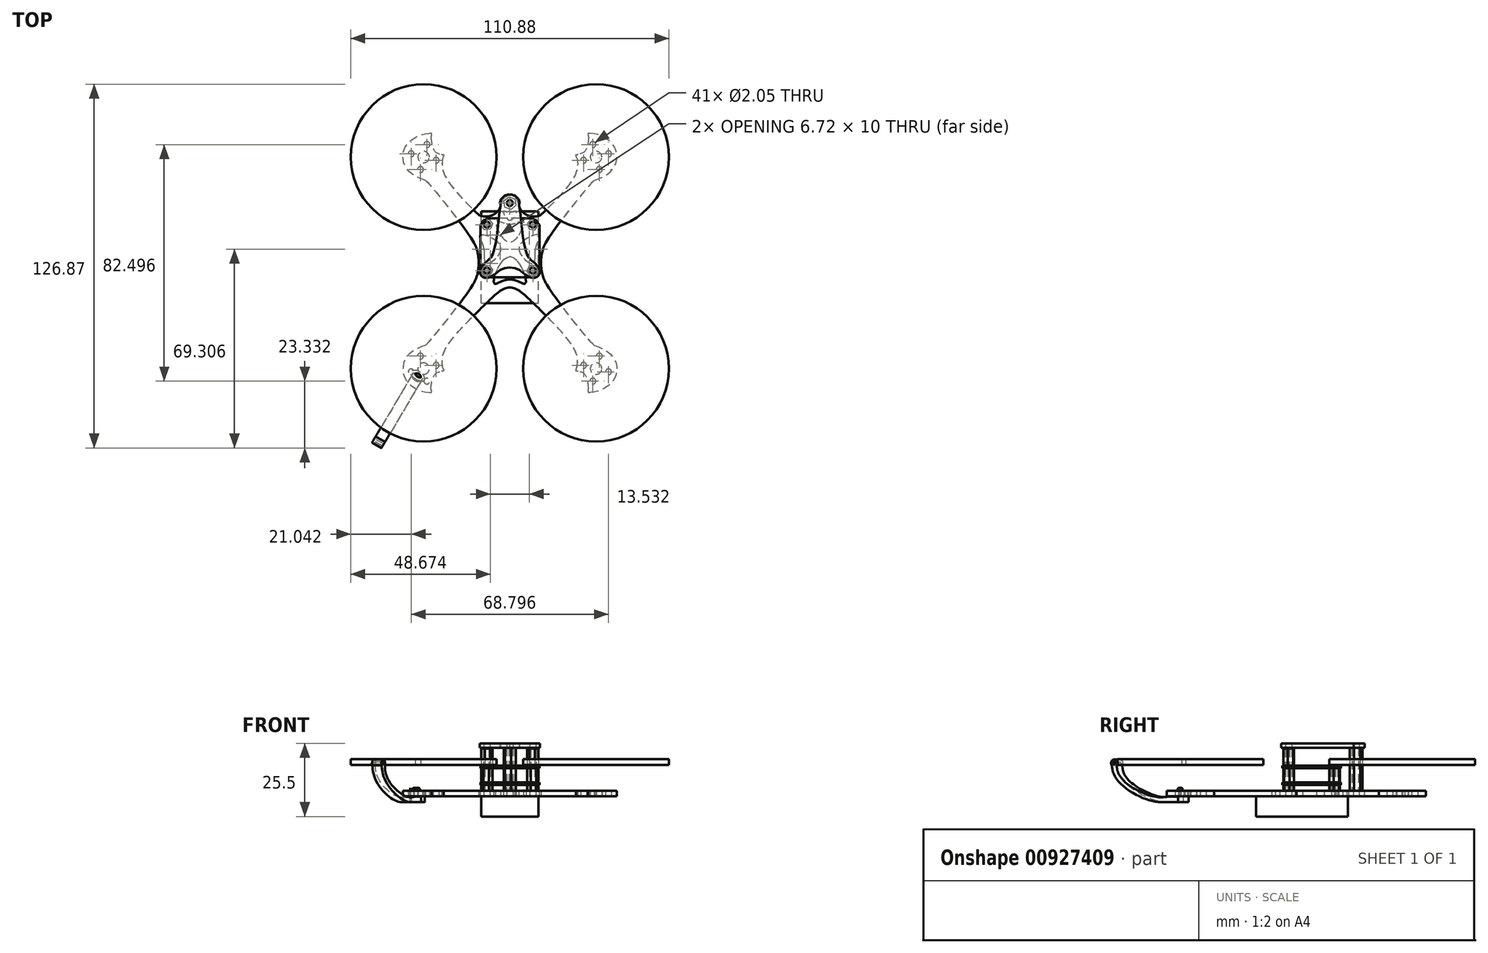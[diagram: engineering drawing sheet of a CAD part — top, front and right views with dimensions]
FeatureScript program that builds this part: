
annotation { "Feature Type Name" : "Feature", "Feature Type Description" : "" }
export const myFeature = defineFeature(function(context is Context, id is Id, definition is map)
    precondition{}
    {
        {
            assignVariable(context, id + "F0", {"name" : "PlateThickness", "anyValue" : 2 * mm});
        }
        {
            assignVariable(context, id + "F1", {"name" : "StackHeight", "lengthValue" : 15 * mm, "variableType" : VariableType.LENGTH});
        }
        {
            assignVariable(context, id + "F2", {"name" : "FCThickness", "anyValue" : 0.85 * mm});
        }
        {
            assignVariable(context, id + "F3", {"name" : "FCSpacerHeight", "anyValue" : 2 * mm});
        }
        {
            assignVariable(context, id + "F4", {"name" : "ESCStandoffHeight", "anyValue" : 5 * mm});
        }
        {
            var Q0;
            Q0=qCreatedBy(makeId("Top.planeOp"),FACE);
            var sketch = newSketch(context, id + "F5", { "sketchPlane" : qUnion([Q0])});
            skLineSegment(sketch, "E0", {"start": v(30.04, 36.9) * mm, "end": v(-30.04, -36.9) * mm, "construction": true});
            skLineSegment(sketch, "E1", {"start": v(-30.04, 36.9) * mm, "end": v(30.04, -36.9) * mm, "construction": true});
            skCircle(sketch, "E2", {"center": v(30.04, 36.9) * mm, "radius": 25.4 * mm, "construction": true});
            skCircle(sketch, "E3", {"center": v(-30.04, 36.9) * mm, "radius": 25.4 * mm, "construction": true});
            skCircle(sketch, "E4", {"center": v(-30.04, -36.9) * mm, "radius": 25.4 * mm, "construction": true});
            skCircle(sketch, "E5", {"center": v(30.04, -36.9) * mm, "radius": 25.4 * mm, "construction": true});
            skLineSegment(sketch, "E6", {"start": v(38.92, 31.66) * mm, "end": v(21.16, 42.12) * mm, "construction": true});
            skLineSegment(sketch, "E7", {"start": v(40.02, 39.47) * mm, "end": v(20.06, 34.31) * mm, "construction": true});
            skLineSegment(sketch, "E8", {"start": v(27.46, 46.87) * mm, "end": v(32.62, 26.91) * mm, "construction": true});
            skCircle(sketch, "E9", {"center": v(30.04, 36.9) * mm, "radius": 4.5 * mm, "construction": true});
            skCircle(sketch, "E10", {"center": v(28.91, 41.25) * mm, "radius": 1.02 * mm});
            skCircle(sketch, "E11", {"center": v(25.68, 35.76) * mm, "radius": 1.02 * mm});
            skCircle(sketch, "E12", {"center": v(31.17, 32.53) * mm, "radius": 1.02 * mm});
            skCircle(sketch, "E13", {"center": v(34.4, 38.02) * mm, "radius": 1.02 * mm});
            skCircle(sketch, "E14", {"center": v(-8, 13.3) * mm, "radius": 1.02 * mm});
            skCircle(sketch, "E15", {"center": v(8, 13.3) * mm, "radius": 1.02 * mm});
            skCircle(sketch, "E16", {"center": v(8, -2.7) * mm, "radius": 1.02 * mm});
            skCircle(sketch, "E17", {"center": v(-8, -2.7) * mm, "radius": 1.02 * mm});
            skCircle(sketch, "E18.MirrorC", {"center": v(-25.68, 35.76) * mm, "radius": 1.02 * mm});
            skCircle(sketch, "E19.MirrorC", {"center": v(-28.91, 41.25) * mm, "radius": 1.02 * mm});
            skCircle(sketch, "E20.MirrorC", {"center": v(-34.4, 38.02) * mm, "radius": 1.02 * mm});
            skCircle(sketch, "E21.MirrorC", {"center": v(-31.17, 32.53) * mm, "radius": 1.02 * mm});
            skCircle(sketch, "E22.MirrorC", {"center": v(-31.17, -32.53) * mm, "radius": 1.02 * mm});
            skCircle(sketch, "E23.MirrorC", {"center": v(-34.4, -38.02) * mm, "radius": 1.02 * mm});
            skCircle(sketch, "E24.MirrorC", {"center": v(-28.91, -41.25) * mm, "radius": 1.02 * mm});
            skCircle(sketch, "E25.MirrorC", {"center": v(-25.68, -35.76) * mm, "radius": 1.02 * mm});
            skCircle(sketch, "E26.MirrorC", {"center": v(25.68, -35.76) * mm, "radius": 1.02 * mm});
            skCircle(sketch, "E27.MirrorC", {"center": v(31.17, -32.53) * mm, "radius": 1.02 * mm});
            skCircle(sketch, "E28.MirrorC", {"center": v(34.4, -38.02) * mm, "radius": 1.02 * mm});
            skCircle(sketch, "E29.MirrorC", {"center": v(28.91, -41.25) * mm, "radius": 1.02 * mm});
            skFitSpline(sketch, "E30", {"points": [v(29.41, 28.73) * mm, v(34.84, 31.56) * mm, v(37.18, 38.3) * mm, v(34.2, 42.9) * mm, v(27.3, 45.15) * mm], "startDerivative": vector(4.7, 2.99) * mm, "endDerivative": vector(-30.23, -2.2) * mm});
            skFitSpline(sketch, "E31", {"points": [v(27.3, 45.15) * mm, v(26.58, 39.57) * mm, v(23, 37.72) * mm], "startDerivative": vector(1.88, -8.22) * mm, "endDerivative": vector(-12.25, -1.45) * mm});
            skFitSpline(sketch, "E32", {"points": [v(23, 37.72) * mm, v(23.04, 31.32) * mm, v(8.78, 14.66) * mm, v(0, 8.59) * mm], "startDerivative": vector(6.6, -21.28) * mm, "endDerivative": vector(-26.5, 0) * mm});
            skFitSpline(sketch, "E33", {"points": [v(29.41, 28.73) * mm, v(14.08, 9.46) * mm, v(10.83, 0) * mm], "startDerivative": vector(-5.44, -3.2) * mm, "endDerivative": vector(-1.35, -29.87) * mm});
            skArc(sketch, "E34.filletArc", {"start": v(28.18, 45.17) * mm, "mid": v(27.62, 44.93) * mm, "end": v(27.41, 44.36) * mm});
            skArc(sketch, "E35.filletArc", {"start": v(23.83, 37.84) * mm, "mid": v(23.33, 37.5) * mm, "end": v(23.24, 36.9) * mm});
            skFitSpline(sketch, "E36.MirrorCS", {"points": [v(29.41, -28.73) * mm, v(14.08, -9.46) * mm, v(10.83, 0) * mm], "startDerivative": vector(-5.44, 3.2) * mm, "endDerivative": vector(-1.35, 29.87) * mm});
            skFitSpline(sketch, "E37.MirrorCS", {"points": [v(23, -37.72) * mm, v(23.04, -31.32) * mm, v(8.78, -14.66) * mm, v(0, -8.59) * mm], "startDerivative": vector(6.6, 21.28) * mm, "endDerivative": vector(-26.5, 0) * mm});
            skArc(sketch, "E38.MirrorCS", {"start": v(23.83, -37.84) * mm, "mid": v(23.33, -37.5) * mm, "end": v(23.24, -36.9) * mm});
            skFitSpline(sketch, "E39.MirrorCS", {"points": [v(27.3, -45.15) * mm, v(26.58, -39.57) * mm, v(23, -37.72) * mm], "startDerivative": vector(1.88, 8.22) * mm, "endDerivative": vector(-12.25, 1.45) * mm});
            skArc(sketch, "E40.MirrorCS", {"start": v(28.18, -45.17) * mm, "mid": v(27.62, -44.93) * mm, "end": v(27.41, -44.36) * mm});
            skFitSpline(sketch, "E41.MirrorCS", {"points": [v(29.41, -28.73) * mm, v(34.84, -31.56) * mm, v(37.18, -38.3) * mm, v(34.2, -42.9) * mm, v(27.3, -45.15) * mm], "startDerivative": vector(4.7, -2.99) * mm, "endDerivative": vector(-30.23, 2.2) * mm});
            skCircle(sketch, "E42", {"center": v(30.04, 36.9) * mm, "radius": 2 * mm});
            skCircle(sketch, "E43.MirrorC", {"center": v(30.04, -36.9) * mm, "radius": 2 * mm});
            skFitSpline(sketch, "E44.MirrorCS", {"points": [v(-29.41, -28.73) * mm, v(-34.84, -31.56) * mm, v(-37.18, -38.3) * mm, v(-34.2, -42.9) * mm, v(-27.3, -45.15) * mm], "startDerivative": vector(-4.7, -2.99) * mm, "endDerivative": vector(30.23, 2.2) * mm});
            skFitSpline(sketch, "E45.MirrorCS", {"points": [v(-27.3, -45.15) * mm, v(-26.58, -39.57) * mm, v(-23, -37.72) * mm], "startDerivative": vector(-1.88, 8.22) * mm, "endDerivative": vector(12.25, 1.45) * mm});
            skArc(sketch, "E46.MirrorCS", {"start": v(-28.18, -45.17) * mm, "mid": v(-27.62, -44.93) * mm, "end": v(-27.41, -44.36) * mm});
            skArc(sketch, "E47.MirrorCS", {"start": v(-23.83, -37.84) * mm, "mid": v(-23.33, -37.5) * mm, "end": v(-23.24, -36.9) * mm});
            skFitSpline(sketch, "E48.MirrorCS", {"points": [v(-23, -37.72) * mm, v(-23.04, -31.32) * mm, v(-8.78, -14.66) * mm, v(0, -8.59) * mm], "startDerivative": vector(-6.6, 21.28) * mm, "endDerivative": vector(26.5, 0) * mm});
            skFitSpline(sketch, "E49.MirrorCS", {"points": [v(-29.41, -28.73) * mm, v(-14.08, -9.46) * mm, v(-10.83, 0) * mm], "startDerivative": vector(5.44, 3.2) * mm, "endDerivative": vector(1.35, 29.87) * mm});
            skCircle(sketch, "E50.MirrorC", {"center": v(-30.04, -36.9) * mm, "radius": 2 * mm});
            skFitSpline(sketch, "E51.MirrorCS", {"points": [v(-29.41, 28.73) * mm, v(-14.08, 9.46) * mm, v(-10.83, 0) * mm], "startDerivative": vector(5.44, -3.2) * mm, "endDerivative": vector(1.35, -29.87) * mm});
            skFitSpline(sketch, "E52.MirrorCS", {"points": [v(-29.41, 28.73) * mm, v(-34.84, 31.56) * mm, v(-37.18, 38.3) * mm, v(-34.2, 42.9) * mm, v(-27.3, 45.15) * mm], "startDerivative": vector(-4.7, 2.99) * mm, "endDerivative": vector(30.23, -2.2) * mm});
            skArc(sketch, "E53.MirrorCS", {"start": v(-28.18, 45.17) * mm, "mid": v(-27.62, 44.93) * mm, "end": v(-27.41, 44.36) * mm});
            skFitSpline(sketch, "E54.MirrorCS", {"points": [v(-27.3, 45.15) * mm, v(-26.58, 39.57) * mm, v(-23, 37.72) * mm], "startDerivative": vector(-1.88, -8.22) * mm, "endDerivative": vector(12.25, -1.45) * mm});
            skArc(sketch, "E55.MirrorCS", {"start": v(-23.83, 37.84) * mm, "mid": v(-23.33, 37.5) * mm, "end": v(-23.24, 36.9) * mm});
            skFitSpline(sketch, "E56.MirrorCS", {"points": [v(-23, 37.72) * mm, v(-23.04, 31.32) * mm, v(-8.78, 14.66) * mm, v(0, 8.59) * mm], "startDerivative": vector(-6.6, -21.28) * mm, "endDerivative": vector(26.5, 0) * mm});
            skCircle(sketch, "E57.MirrorC", {"center": v(-30.04, 36.9) * mm, "radius": 2 * mm});
            skFitSpline(sketch, "E58", {"points": [v(10.08, 9.75) * mm, v(3.22, 5.3) * mm, v(8.08, -0.3) * mm, v(9, 4.92) * mm, v(10.08, 9.75) * mm]});
            skFitSpline(sketch, "E59.MirrorC", {"points": [v(-10.08, 9.75) * mm, v(-3.22, 5.3) * mm, v(-8.08, -0.3) * mm, v(-9, 4.92) * mm, v(-10.08, 9.75) * mm]});
            skFitSpline(sketch, "E60.MirrorC", {"points": [v(0, 2.19) * mm, v(5.5, -7.02) * mm, v(0, -5.75) * mm, v(-5.5, -7.02) * mm, v(0, 2.19) * mm]});
            skFitSpline(sketch, "E61", {"points": [v(31.89, 39.83) * mm, v(34.14, 40.16) * mm, v(32.64, 42.18) * mm, v(30.86, 42.04) * mm, v(31.89, 39.83) * mm], "construction": true});
            skFitSpline(sketch, "E62", {"points": [v(33.63, 36.26) * mm, v(32.54, 35.08) * mm, v(33.08, 33.36) * mm, v(34.42, 34.31) * mm, v(34.82, 35.96) * mm, v(33.63, 36.26) * mm], "construction": true});
            skLineSegment(sketch, "E63", {"start": v(17.83, 16.16) * mm, "end": v(35.03, 45.37) * mm, "construction": true});
            skFitSpline(sketch, "E64.MirrorC", {"points": [v(-31.89, 39.83) * mm, v(-34.14, 40.16) * mm, v(-32.64, 42.18) * mm, v(-30.86, 42.04) * mm, v(-31.89, 39.83) * mm], "construction": true});
            skFitSpline(sketch, "E65.MirrorC", {"points": [v(-33.63, 36.26) * mm, v(-32.54, 35.08) * mm, v(-33.08, 33.36) * mm, v(-34.42, 34.31) * mm, v(-34.82, 35.96) * mm, v(-33.63, 36.26) * mm], "construction": true});
            skFitSpline(sketch, "E66.MirrorC", {"points": [v(33.63, -36.26) * mm, v(32.54, -35.08) * mm, v(33.08, -33.36) * mm, v(34.42, -34.31) * mm, v(34.82, -35.96) * mm, v(33.63, -36.26) * mm], "construction": true});
            skFitSpline(sketch, "E67.MirrorC", {"points": [v(31.89, -39.83) * mm, v(34.14, -40.16) * mm, v(32.64, -42.18) * mm, v(30.86, -42.04) * mm, v(31.89, -39.83) * mm], "construction": true});
            skFitSpline(sketch, "E68.MirrorC", {"points": [v(-31.89, -39.83) * mm, v(-34.14, -40.16) * mm, v(-32.64, -42.18) * mm, v(-30.86, -42.04) * mm, v(-31.89, -39.83) * mm], "construction": true});
            skFitSpline(sketch, "E69.MirrorC", {"points": [v(-33.63, -36.26) * mm, v(-32.54, -35.08) * mm, v(-33.08, -33.36) * mm, v(-34.42, -34.31) * mm, v(-34.82, -35.96) * mm, v(-33.63, -36.26) * mm], "construction": true});
            skCircle(sketch, "E70", {"center": v(0, 20.84) * mm, "radius": 1.02 * mm});
            skFitSpline(sketch, "E71", {"points": [v(-11.69, 17.5) * mm, v(-4.28, 17.9) * mm, v(-2.63, 21.6) * mm, v(0, 23.7) * mm], "startDerivative": vector(17.88, -17.8) * mm, "endDerivative": vector(10.8, -0.04) * mm});
            skFitSpline(sketch, "E72.MirrorCS", {"points": [v(11.69, 17.5) * mm, v(4.28, 17.9) * mm, v(2.63, 21.6) * mm, v(0, 23.7) * mm], "startDerivative": vector(-17.88, -17.8) * mm, "endDerivative": vector(-10.8, -0.04) * mm});
            skLineSegment(sketch, "E73", {"start": v(27.93, 47.57) * mm, "end": v(40.4, 40.22) * mm, "construction": true});
            skPoint(sketch, "E74", {"position": v(34.17, 43.9) * mm});
            skLineSegment(sketch, "E75", {"start": v(40.4, 40.22) * mm, "end": v(33.06, 27.74) * mm, "construction": true});
            skLineSegment(sketch, "E76", {"start": v(27.93, 47.57) * mm, "end": v(20.58, 35.1) * mm, "construction": true});
            skLineSegment(sketch, "E77", {"start": v(33.06, 27.74) * mm, "end": v(20.58, 35.1) * mm, "construction": true});
            skLineSegment(sketch, "E78", {"start": v(8, 13.3) * mm, "end": v(-8, -2.7) * mm, "construction": true});
            skLineSegment(sketch, "E79", {"start": v(8, -2.7) * mm, "end": v(-8, 13.3) * mm, "construction": true});
            skPoint(sketch, "E80", {"position": v(0, 5.3) * mm});
            skLineSegment(sketch, "E81", {"start": v(-2.38, 5.3) * mm, "end": v(2.38, 5.3) * mm, "construction": true});
            skFitSpline(sketch, "E82.MirrorC", {"points": [v(0, 7.2) * mm, v(4.88, 14.48) * mm, v(0, 13.35) * mm, v(-4.88, 14.48) * mm, v(0, 7.2) * mm]});
            skFitSpline(sketch, "E83", {"points": [v(0, 17.57) * mm, v(2.16, 18.06) * mm, v(0, 14.71) * mm, v(-2.16, 18.06) * mm, v(0, 17.57) * mm]});
            skFitSpline(sketch, "E84", {"points": [v(-8.8, 1.66) * mm, v(-7.94, 2.3) * mm, v(-6.94, 1.65) * mm, v(-6.44, 3.35) * mm, v(-6.94, 5.05) * mm, v(-7.94, 4.4) * mm, v(-8.94, 4.63) * mm], "startDerivative": vector(0.09, 5.2) * mm, "endDerivative": vector(-0.67, 5.38) * mm});
            skLineSegment(sketch, "E85", {"start": v(-6.2, 3.35) * mm, "end": v(-9.6, 3.35) * mm, "construction": true});
            skFitSpline(sketch, "E86.MirrorCS", {"points": [v(8.8, 1.66) * mm, v(7.94, 2.3) * mm, v(6.94, 1.65) * mm, v(6.44, 3.35) * mm, v(6.94, 5.05) * mm, v(7.94, 4.4) * mm, v(8.94, 4.63) * mm], "startDerivative": vector(-0.09, 5.2) * mm, "endDerivative": vector(0.67, 5.38) * mm});
            skFitSpline(sketch, "E87", {"points": [v(1.82, -6.1) * mm, v(1.05, -5.1) * mm, v(1.7, -4.1) * mm, v(0, -3.6) * mm, v(-1.7, -4.1) * mm, v(-1.05, -5.1) * mm, v(-1.82, -6.1) * mm], "startDerivative": vector(-10.77, 5.24) * mm, "endDerivative": vector(-10.77, -5.24) * mm});
            skFitSpline(sketch, "E88", {"points": [v(-1.82, 13.7) * mm, v(-1.05, 12.7) * mm, v(-1.7, 11.7) * mm, v(0, 11.2) * mm, v(1.7, 11.7) * mm, v(1.05, 12.7) * mm, v(1.82, 13.7) * mm], "startDerivative": vector(3.97, -1.14) * mm, "endDerivative": vector(3.92, 1.03) * mm});
            skCircle(sketch, "E89", {"center": v(30.04, 36.9) * mm, "radius": 6.75 * mm, "construction": true});
            skSolve(sketch);
        }
        {
            var Q0;
            Q0=qSketchRegion(id+"F5",true);
            extrude(context, id + "F6", {"entities" : qUnion([Q0]), "depth" : getVariable(context, 'PlateThickness'), "offsetDistance" : 25 * mm});
        }
        {
            var Q0;
            Q0=makeQuery(id+"F6.opExtrude","CAP_FACE",FACE,{"disambiguationData":[OSD([sQuery(id+"F5.wireOp",EDGE,"E10"),sQuery(id+"F5.wireOp",EDGE,"E11"),sQuery(id+"F5.wireOp",EDGE,"E12"),sQuery(id+"F5.wireOp",EDGE,"E13"),sQuery(id+"F5.wireOp",EDGE,"E14"),sQuery(id+"F5.wireOp",EDGE,"E15"),sQuery(id+"F5.wireOp",EDGE,"E16"),sQuery(id+"F5.wireOp",EDGE,"E17"),sQuery(id+"F5.wireOp",EDGE,"E18.MirrorC"),sQuery(id+"F5.wireOp",EDGE,"E19.MirrorC"),sQuery(id+"F5.wireOp",EDGE,"E20.MirrorC"),sQuery(id+"F5.wireOp",EDGE,"E21.MirrorC"),sQuery(id+"F5.wireOp",EDGE,"E25.MirrorC"),sQuery(id+"F5.wireOp",EDGE,"E26.MirrorC"),sQuery(id+"F5.wireOp",EDGE,"E27.MirrorC"),sQuery(id+"F5.wireOp",EDGE,"E28.MirrorC"),sQuery(id+"F5.wireOp",EDGE,"E29.MirrorC"),sQuery(id+"F5.wireOp",EDGE,"E30"),sQuery(id+"F5.wireOp",EDGE,"E31"),sQuery(id+"F5.wireOp",EDGE,"E32"),sQuery(id+"F5.wireOp",EDGE,"E33"),sQuery(id+"F5.wireOp",EDGE,"E34.filletArc"),sQuery(id+"F5.wireOp",EDGE,"E35.filletArc"),sQuery(id+"F5.wireOp",EDGE,"E36.MirrorCS"),sQuery(id+"F5.wireOp",EDGE,"E37.MirrorCS"),sQuery(id+"F5.wireOp",EDGE,"E38.MirrorCS"),sQuery(id+"F5.wireOp",EDGE,"E39.MirrorCS"),sQuery(id+"F5.wireOp",EDGE,"E40.MirrorCS"),sQuery(id+"F5.wireOp",EDGE,"E41.MirrorCS"),sQuery(id+"F5.wireOp",EDGE,"E42"),sQuery(id+"F5.wireOp",EDGE,"E43.MirrorC"),sQuery(id+"F5.wireOp",EDGE,"E23.MirrorC"),sQuery(id+"F5.wireOp",EDGE,"E44.MirrorCS"),sQuery(id+"F5.wireOp",EDGE,"E22.MirrorC"),sQuery(id+"F5.wireOp",EDGE,"E24.MirrorC"),sQuery(id+"F5.wireOp",EDGE,"E45.MirrorCS"),sQuery(id+"F5.wireOp",EDGE,"E46.MirrorCS"),sQuery(id+"F5.wireOp",EDGE,"E47.MirrorCS"),sQuery(id+"F5.wireOp",EDGE,"E48.MirrorCS"),sQuery(id+"F5.wireOp",EDGE,"E49.MirrorCS"),sQuery(id+"F5.wireOp",EDGE,"E50.MirrorC"),sQuery(id+"F5.wireOp",EDGE,"E51.MirrorCS"),sQuery(id+"F5.wireOp",EDGE,"E52.MirrorCS"),sQuery(id+"F5.wireOp",EDGE,"E53.MirrorCS"),sQuery(id+"F5.wireOp",EDGE,"E54.MirrorCS"),sQuery(id+"F5.wireOp",EDGE,"E55.MirrorCS"),sQuery(id+"F5.wireOp",EDGE,"E56.MirrorCS"),sQuery(id+"F5.wireOp",EDGE,"E57.MirrorC"),sQuery(id+"F5.wireOp",EDGE,"E58"),sQuery(id+"F5.wireOp",EDGE,"E59.MirrorC"),sQuery(id+"F5.wireOp",EDGE,"dcd4970c-f5e5-4935-b7b6-60d1fb3fb8a0"),sQuery(id+"F5.wireOp",EDGE,"E60.MirrorC"),sQuery(id+"F5.wireOp",EDGE,"E61"),sQuery(id+"F5.wireOp",EDGE,"E62")])],"isStart":false});
            var sketch = newSketch(context, id + "F7", { "sketchPlane" : qUnion([Q0])});
            skCircle(sketch, "E90.cCircle", {"center": v(-8, 13.3) * mm, "radius": 2 * mm, "construction": true});
            skLineSegment(sketch, "E90.0", {"start": v(-9.24, 14.88) * mm, "end": v(-7.26, 15.16) * mm});
            skLineSegment(sketch, "E90.1", {"start": v(-7.26, 15.16) * mm, "end": v(-6.02, 13.59) * mm});
            skLineSegment(sketch, "E90.2", {"start": v(-6.02, 13.59) * mm, "end": v(-6.76, 11.73) * mm});
            skLineSegment(sketch, "E90.3", {"start": v(-6.76, 11.73) * mm, "end": v(-8.74, 11.45) * mm});
            skLineSegment(sketch, "E90.4", {"start": v(-8.74, 11.45) * mm, "end": v(-9.98, 13.02) * mm});
            skLineSegment(sketch, "E90.5", {"start": v(-9.98, 13.02) * mm, "end": v(-9.24, 14.88) * mm});
            skLineSegment(sketch, "E91.MirrorCS", {"start": v(9.98, 13.02) * mm, "end": v(9.24, 14.88) * mm});
            skLineSegment(sketch, "E92.MirrorCS", {"start": v(7.26, 15.16) * mm, "end": v(6.02, 13.59) * mm});
            skLineSegment(sketch, "E93.MirrorCS", {"start": v(6.02, 13.59) * mm, "end": v(6.76, 11.73) * mm});
            skCircle(sketch, "E94.MirrorC", {"center": v(8, 13.3) * mm, "radius": 2 * mm, "construction": true});
            skLineSegment(sketch, "E95.MirrorCS", {"start": v(8.74, 11.45) * mm, "end": v(9.98, 13.02) * mm});
            skLineSegment(sketch, "E96.MirrorCS", {"start": v(6.76, 11.73) * mm, "end": v(8.74, 11.45) * mm});
            skLineSegment(sketch, "E97.MirrorCS", {"start": v(9.24, 14.88) * mm, "end": v(7.26, 15.16) * mm});
            skCircle(sketch, "E98.0", {"center": v(-8, 13.3) * mm, "radius": 1.02 * mm});
            skCircle(sketch, "E99.0", {"center": v(8, 13.3) * mm, "radius": 1.02 * mm});
            skCircle(sketch, "E100.0", {"center": v(8, -2.7) * mm, "radius": 1.02 * mm});
            skCircle(sketch, "E101.0", {"center": v(-8, -2.7) * mm, "radius": 1.02 * mm});
            skLineSegment(sketch, "E102.MirrorCS", {"start": v(-9.24, -4.27) * mm, "end": v(-7.26, -4.55) * mm});
            skLineSegment(sketch, "E103.MirrorCS", {"start": v(-9.98, -2.41) * mm, "end": v(-9.24, -4.27) * mm});
            skLineSegment(sketch, "E104.MirrorCS", {"start": v(-7.26, -4.55) * mm, "end": v(-6.02, -2.98) * mm});
            skLineSegment(sketch, "E105.MirrorCS", {"start": v(-6.02, -2.98) * mm, "end": v(-6.76, -1.12) * mm});
            skLineSegment(sketch, "E106.MirrorCS", {"start": v(-6.76, -1.12) * mm, "end": v(-8.74, -0.84) * mm});
            skLineSegment(sketch, "E107.MirrorCS", {"start": v(-8.74, -0.84) * mm, "end": v(-9.98, -2.41) * mm});
            skLineSegment(sketch, "E108.MirrorCS", {"start": v(7.26, -4.55) * mm, "end": v(6.02, -2.98) * mm});
            skLineSegment(sketch, "E109.MirrorCS", {"start": v(9.24, -4.27) * mm, "end": v(7.26, -4.55) * mm});
            skLineSegment(sketch, "E110.MirrorCS", {"start": v(9.98, -2.41) * mm, "end": v(9.24, -4.27) * mm});
            skLineSegment(sketch, "E111.MirrorCS", {"start": v(8.74, -0.84) * mm, "end": v(9.98, -2.41) * mm});
            skLineSegment(sketch, "E112.MirrorCS", {"start": v(6.76, -1.12) * mm, "end": v(8.74, -0.84) * mm});
            skLineSegment(sketch, "E113.MirrorCS", {"start": v(6.02, -2.98) * mm, "end": v(6.76, -1.12) * mm});
            skSolve(sketch);
        }
        {
            var Q0;
            Q0=qSketchRegion(id+"F7",true);
            extrude(context, id + "F8", {"entities" : qUnion([Q0]), "depth" : getVariable(context, 'FCSpacerHeight'), "offsetDistance" : 25 * mm});
        }
        {
            var Q0;
            Q0=makeQuery(id+"F6.opExtrude","CAP_FACE",FACE,{"disambiguationData":[OSD([sQuery(id+"F5.wireOp",EDGE,"E10"),sQuery(id+"F5.wireOp",EDGE,"E11"),sQuery(id+"F5.wireOp",EDGE,"E12"),sQuery(id+"F5.wireOp",EDGE,"E13"),sQuery(id+"F5.wireOp",EDGE,"E14"),sQuery(id+"F5.wireOp",EDGE,"E15"),sQuery(id+"F5.wireOp",EDGE,"E16"),sQuery(id+"F5.wireOp",EDGE,"E17"),sQuery(id+"F5.wireOp",EDGE,"E18.MirrorC"),sQuery(id+"F5.wireOp",EDGE,"E19.MirrorC"),sQuery(id+"F5.wireOp",EDGE,"E20.MirrorC"),sQuery(id+"F5.wireOp",EDGE,"E21.MirrorC"),sQuery(id+"F5.wireOp",EDGE,"E25.MirrorC"),sQuery(id+"F5.wireOp",EDGE,"E26.MirrorC"),sQuery(id+"F5.wireOp",EDGE,"E27.MirrorC"),sQuery(id+"F5.wireOp",EDGE,"E28.MirrorC"),sQuery(id+"F5.wireOp",EDGE,"E29.MirrorC"),sQuery(id+"F5.wireOp",EDGE,"E30"),sQuery(id+"F5.wireOp",EDGE,"E31"),sQuery(id+"F5.wireOp",EDGE,"E32"),sQuery(id+"F5.wireOp",EDGE,"E33"),sQuery(id+"F5.wireOp",EDGE,"E34.filletArc"),sQuery(id+"F5.wireOp",EDGE,"E35.filletArc"),sQuery(id+"F5.wireOp",EDGE,"E36.MirrorCS"),sQuery(id+"F5.wireOp",EDGE,"E37.MirrorCS"),sQuery(id+"F5.wireOp",EDGE,"E38.MirrorCS"),sQuery(id+"F5.wireOp",EDGE,"E39.MirrorCS"),sQuery(id+"F5.wireOp",EDGE,"E40.MirrorCS"),sQuery(id+"F5.wireOp",EDGE,"E41.MirrorCS"),sQuery(id+"F5.wireOp",EDGE,"E42"),sQuery(id+"F5.wireOp",EDGE,"E43.MirrorC"),sQuery(id+"F5.wireOp",EDGE,"E23.MirrorC"),sQuery(id+"F5.wireOp",EDGE,"E44.MirrorCS"),sQuery(id+"F5.wireOp",EDGE,"E22.MirrorC"),sQuery(id+"F5.wireOp",EDGE,"E24.MirrorC"),sQuery(id+"F5.wireOp",EDGE,"E45.MirrorCS"),sQuery(id+"F5.wireOp",EDGE,"E46.MirrorCS"),sQuery(id+"F5.wireOp",EDGE,"E47.MirrorCS"),sQuery(id+"F5.wireOp",EDGE,"E48.MirrorCS"),sQuery(id+"F5.wireOp",EDGE,"E49.MirrorCS"),sQuery(id+"F5.wireOp",EDGE,"E50.MirrorC"),sQuery(id+"F5.wireOp",EDGE,"E51.MirrorCS"),sQuery(id+"F5.wireOp",EDGE,"E52.MirrorCS"),sQuery(id+"F5.wireOp",EDGE,"E53.MirrorCS"),sQuery(id+"F5.wireOp",EDGE,"E54.MirrorCS"),sQuery(id+"F5.wireOp",EDGE,"E55.MirrorCS"),sQuery(id+"F5.wireOp",EDGE,"E56.MirrorCS"),sQuery(id+"F5.wireOp",EDGE,"E57.MirrorC"),sQuery(id+"F5.wireOp",EDGE,"E58"),sQuery(id+"F5.wireOp",EDGE,"E59.MirrorC"),sQuery(id+"F5.wireOp",EDGE,"dcd4970c-f5e5-4935-b7b6-60d1fb3fb8a0"),sQuery(id+"F5.wireOp",EDGE,"E60.MirrorC"),sQuery(id+"F5.wireOp",EDGE,"E61"),sQuery(id+"F5.wireOp",EDGE,"E62"),sQuery(id+"F5.wireOp",EDGE,"E64.MirrorC"),sQuery(id+"F5.wireOp",EDGE,"E65.MirrorC"),sQuery(id+"F5.wireOp",EDGE,"E66.MirrorC"),sQuery(id+"F5.wireOp",EDGE,"E67.MirrorC"),sQuery(id+"F5.wireOp",EDGE,"E68.MirrorC"),sQuery(id+"F5.wireOp",EDGE,"E69.MirrorC"),sQuery(id+"F5.wireOp",EDGE,"E70"),sQuery(id+"F5.wireOp",EDGE,"E71"),sQuery(id+"F5.wireOp",EDGE,"E72.MirrorCS"),sQuery(id+"F5.wireOp",EDGE,"54bec6d1-b576-4d2f-8366-efb064a77230")])],"isStart":false});
            var sketch = newSketch(context, id + "F9", { "sketchPlane" : qUnion([Q0])});
            skCircle(sketch, "E114.0", {"center": v(0, 20.84) * mm, "radius": 1.02 * mm});
            skCircle(sketch, "E115.cCircle", {"center": v(0, 20.84) * mm, "radius": 2.25 * mm, "construction": true});
            skLineSegment(sketch, "E115.0", {"start": v(-1.73, 19.4) * mm, "end": v(-2.11, 21.62) * mm});
            skLineSegment(sketch, "E115.1", {"start": v(-2.11, 21.62) * mm, "end": v(-0.38, 23.06) * mm});
            skLineSegment(sketch, "E115.2", {"start": v(-0.38, 23.06) * mm, "end": v(1.73, 22.28) * mm});
            skLineSegment(sketch, "E115.3", {"start": v(1.73, 22.28) * mm, "end": v(2.11, 20.06) * mm});
            skLineSegment(sketch, "E115.4", {"start": v(2.11, 20.06) * mm, "end": v(0.38, 18.62) * mm});
            skLineSegment(sketch, "E115.5", {"start": v(0.38, 18.62) * mm, "end": v(-1.73, 19.4) * mm});
            skSolve(sketch);
        }
        {
            var Q0;
            Q0=makeQuery(id+"F9.imprint","IMPRINT",FACE,{"disambiguationData":[TD([[makeQuery(id+"F9.imprint","IMPRINT",EDGE,{"derivedFrom":sQuery(id+"F9.wireOp",EDGE,"E114.0")}),-1.0]])]});
            extrude(context, id + "F10", {"entities" : qUnion([Q0]), "depth" : getVariable(context, 'StackHeight'), "offsetDistance" : 25 * mm});
        }
        {
            var Q0;
            Q0=makeQuery(id+"F8.opExtrude","CAP_FACE",FACE,{"disambiguationData":[OSD([sQuery(id+"F7.wireOp",EDGE,"E90.0"),sQuery(id+"F7.wireOp",EDGE,"E90.1"),sQuery(id+"F7.wireOp",EDGE,"E90.2"),sQuery(id+"F7.wireOp",EDGE,"E90.3"),sQuery(id+"F7.wireOp",EDGE,"E90.4"),sQuery(id+"F7.wireOp",EDGE,"E90.5"),sQuery(id+"F7.wireOp",EDGE,"E98.0")])],"isStart":false});
            var sketch = newSketch(context, id + "F11", { "sketchPlane" : qUnion([Q0])});
            skLineSegment(sketch, "E116", {"start": v(0, 15.59) * mm, "end": v(0, -11.41) * mm, "construction": true});
            skLineSegment(sketch, "E117", {"start": v(-10.29, 5.3) * mm, "end": v(16.71, 5.3) * mm, "construction": true});
            skLineSegment(sketch, "E118", {"start": v(-10.29, 13.3) * mm, "end": v(-10.29, -2.7) * mm});
            skLineSegment(sketch, "E119", {"start": v(8, 15.59) * mm, "end": v(-8, 15.59) * mm});
            skLineSegment(sketch, "E120.MirrorCS", {"start": v(8, -4.98) * mm, "end": v(-8, -4.98) * mm});
            skLineSegment(sketch, "E121.MirrorCS", {"start": v(10.29, 13.3) * mm, "end": v(10.29, -2.7) * mm});
            skLineSegment(sketch, "E122", {"start": v(-8, 15.59) * mm, "end": v(-10.29, 13.3) * mm});
            skLineSegment(sketch, "E123.MirrorCS", {"start": v(-8, -4.98) * mm, "end": v(-10.29, -2.7) * mm});
            skLineSegment(sketch, "E124.MirrorCS", {"start": v(8, 15.59) * mm, "end": v(10.29, 13.3) * mm});
            skLineSegment(sketch, "E125.MirrorCS", {"start": v(8, -4.98) * mm, "end": v(10.29, -2.7) * mm});
            skCircle(sketch, "E126", {"center": v(-8, 13.3) * mm, "radius": 1.02 * mm});
            skLineSegment(sketch, "E127", {"start": v(-8, 13.3) * mm, "end": v(8, 13.3) * mm, "construction": true});
            skLineSegment(sketch, "E128", {"start": v(8, 13.3) * mm, "end": v(8, -2.7) * mm, "construction": true});
            skLineSegment(sketch, "E129", {"start": v(8, -2.7) * mm, "end": v(-8, -2.7) * mm, "construction": true});
            skLineSegment(sketch, "E130", {"start": v(-8, -2.7) * mm, "end": v(-8, 13.3) * mm, "construction": true});
            skPoint(sketch, "E131", {"position": v(0, 13.3) * mm});
            skPoint(sketch, "E132", {"position": v(-8, 5.3) * mm});
            skCircle(sketch, "E133.MirrorC", {"center": v(8, 13.3) * mm, "radius": 1.02 * mm});
            skCircle(sketch, "E134.MirrorC", {"center": v(-8, -2.7) * mm, "radius": 1.02 * mm});
            skCircle(sketch, "E135.MirrorC", {"center": v(8, -2.7) * mm, "radius": 1.02 * mm});
            skSolve(sketch);
        }
        {
            var Q0;
            Q0=qSketchRegion(id+"F11",true);
            extrude(context, id + "F12", {"entities" : qUnion([Q0]), "depth" : getVariable(context, 'FCThickness'), "offsetDistance" : 25 * mm});
        }
        {
            var Q0;
            Q0=makeQuery(id+"F12.opExtrude","CAP_FACE",FACE,{"disambiguationData":[OSD([sQuery(id+"F11.wireOp",EDGE,"E118"),sQuery(id+"F11.wireOp",EDGE,"E119"),sQuery(id+"F11.wireOp",EDGE,"E120.MirrorCS"),sQuery(id+"F11.wireOp",EDGE,"E121.MirrorCS"),sQuery(id+"F11.wireOp",EDGE,"E122"),sQuery(id+"F11.wireOp",EDGE,"E123.MirrorCS"),sQuery(id+"F11.wireOp",EDGE,"E124.MirrorCS"),sQuery(id+"F11.wireOp",EDGE,"E125.MirrorCS"),sQuery(id+"F11.wireOp",EDGE,"E126"),sQuery(id+"F11.wireOp",EDGE,"E133.MirrorC"),sQuery(id+"F11.wireOp",EDGE,"E134.MirrorC"),sQuery(id+"F11.wireOp",EDGE,"E135.MirrorC")])],"isStart":false});
            var sketch = newSketch(context, id + "F13", { "sketchPlane" : qUnion([Q0])});
            skLineSegment(sketch, "E136.0", {"start": v(-9.24, 14.88) * mm, "end": v(-7.26, 15.16) * mm});
            skLineSegment(sketch, "E137.0", {"start": v(-9.98, 13.02) * mm, "end": v(-9.24, 14.88) * mm});
            skLineSegment(sketch, "E138.0", {"start": v(-8.74, 11.45) * mm, "end": v(-9.98, 13.02) * mm});
            skLineSegment(sketch, "E139.0", {"start": v(-6.76, 11.73) * mm, "end": v(-8.74, 11.45) * mm});
            skLineSegment(sketch, "E140.0", {"start": v(-6.02, 13.59) * mm, "end": v(-6.76, 11.73) * mm});
            skLineSegment(sketch, "E141.0", {"start": v(-7.26, 15.16) * mm, "end": v(-6.02, 13.59) * mm});
            skCircle(sketch, "E142.0", {"center": v(-8, 13.3) * mm, "radius": 1.02 * mm});
            skCircle(sketch, "E143.0", {"center": v(8, 13.3) * mm, "radius": 1.02 * mm});
            skLineSegment(sketch, "E144.0", {"start": v(9.24, 14.88) * mm, "end": v(7.26, 15.16) * mm});
            skLineSegment(sketch, "E145.0", {"start": v(9.98, 13.02) * mm, "end": v(9.24, 14.88) * mm});
            skLineSegment(sketch, "E146.0", {"start": v(8.74, 11.45) * mm, "end": v(9.98, 13.02) * mm});
            skLineSegment(sketch, "E147.0", {"start": v(6.76, 11.73) * mm, "end": v(8.74, 11.45) * mm});
            skLineSegment(sketch, "E148.0", {"start": v(6.02, 13.59) * mm, "end": v(6.76, 11.73) * mm});
            skLineSegment(sketch, "E149.0", {"start": v(7.26, 15.16) * mm, "end": v(6.02, 13.59) * mm});
            skLineSegment(sketch, "E150.0", {"start": v(-6.76, -1.12) * mm, "end": v(-8.74, -0.84) * mm});
            skLineSegment(sketch, "E151.0", {"start": v(-6.02, -2.98) * mm, "end": v(-6.76, -1.12) * mm});
            skLineSegment(sketch, "E152.0", {"start": v(-7.26, -4.55) * mm, "end": v(-6.02, -2.98) * mm});
            skLineSegment(sketch, "E153.0", {"start": v(-9.24, -4.27) * mm, "end": v(-7.26, -4.55) * mm});
            skLineSegment(sketch, "E154.0", {"start": v(-9.98, -2.41) * mm, "end": v(-9.24, -4.27) * mm});
            skLineSegment(sketch, "E155.0", {"start": v(-8.74, -0.84) * mm, "end": v(-9.98, -2.41) * mm});
            skCircle(sketch, "E156.0", {"center": v(-8, -2.7) * mm, "radius": 1.02 * mm});
            skCircle(sketch, "E157.0", {"center": v(8, -2.7) * mm, "radius": 1.02 * mm});
            skLineSegment(sketch, "E158.0", {"start": v(6.02, -2.98) * mm, "end": v(6.76, -1.12) * mm});
            skLineSegment(sketch, "E159.0", {"start": v(7.26, -4.55) * mm, "end": v(6.02, -2.98) * mm});
            skLineSegment(sketch, "E160.0", {"start": v(9.24, -4.27) * mm, "end": v(7.26, -4.55) * mm});
            skLineSegment(sketch, "E161.0", {"start": v(9.98, -2.41) * mm, "end": v(9.24, -4.27) * mm});
            skLineSegment(sketch, "E162.0", {"start": v(8.74, -0.84) * mm, "end": v(9.98, -2.41) * mm});
            skLineSegment(sketch, "E163.0", {"start": v(6.76, -1.12) * mm, "end": v(8.74, -0.84) * mm});
            skSolve(sketch);
        }
        {
            var Q0;
            Q0=qSketchRegion(id+"F13",true);
            extrude(context, id + "F14", {"entities" : qUnion([Q0]), "depth" : getVariable(context, 'ESCStandoffHeight'), "offsetDistance" : 25 * mm});
        }
        {
            var Q0;
            Q0=makeQuery(id+"F14.opExtrude","CAP_FACE",FACE,{"disambiguationData":[OSD([sQuery(id+"F13.wireOp",EDGE,"E136.0"),sQuery(id+"F13.wireOp",EDGE,"E137.0"),sQuery(id+"F13.wireOp",EDGE,"E138.0"),sQuery(id+"F13.wireOp",EDGE,"E139.0"),sQuery(id+"F13.wireOp",EDGE,"E140.0"),sQuery(id+"F13.wireOp",EDGE,"E141.0"),sQuery(id+"F13.wireOp",EDGE,"E142.0")])],"isStart":false});
            var sketch = newSketch(context, id + "F15", { "sketchPlane" : qUnion([Q0])});
            skCircle(sketch, "E164.0", {"center": v(8, -2.7) * mm, "radius": 1.02 * mm});
            skLineSegment(sketch, "E164.1", {"start": v(8, 15.59) * mm, "end": v(-8, 15.59) * mm});
            skCircle(sketch, "E164.2", {"center": v(8, 13.3) * mm, "radius": 1.02 * mm});
            skCircle(sketch, "E164.3", {"center": v(-8, -2.7) * mm, "radius": 1.02 * mm});
            skCircle(sketch, "E164.6", {"center": v(-8, 13.3) * mm, "radius": 1.02 * mm});
            skLineSegment(sketch, "E164.9", {"start": v(-10.29, 13.3) * mm, "end": v(-10.29, -2.7) * mm});
            skLineSegment(sketch, "E164.10", {"start": v(8, 15.59) * mm, "end": v(10.29, 13.3) * mm});
            skLineSegment(sketch, "E164.11", {"start": v(8, -4.98) * mm, "end": v(10.29, -2.7) * mm});
            skLineSegment(sketch, "E164.12", {"start": v(8, -4.98) * mm, "end": v(-8, -4.98) * mm});
            skLineSegment(sketch, "E164.13", {"start": v(-8, -4.98) * mm, "end": v(-10.29, -2.7) * mm});
            skLineSegment(sketch, "E164.14", {"start": v(-8, 15.59) * mm, "end": v(-10.29, 13.3) * mm});
            skLineSegment(sketch, "E164.17", {"start": v(10.29, 13.3) * mm, "end": v(10.29, -2.7) * mm});
            skSolve(sketch);
        }
        {
            var Q0;
            Q0=qSketchRegion(id+"F15",true);
            extrude(context, id + "F16", {"entities" : qUnion([Q0]), "depth" : getVariable(context, 'FCThickness'), "offsetDistance" : 25 * mm});
        }
        {
            var Q0;
            Q0=makeQuery(id+"F16.opExtrude","CAP_FACE",FACE,{"disambiguationData":[OSD([sQuery(id+"F15.wireOp",EDGE,"E164.0"),sQuery(id+"F15.wireOp",EDGE,"E164.1"),sQuery(id+"F15.wireOp",EDGE,"E164.2"),sQuery(id+"F15.wireOp",EDGE,"E164.3"),sQuery(id+"F15.wireOp",EDGE,"E164.6"),sQuery(id+"F15.wireOp",EDGE,"E164.9"),sQuery(id+"F15.wireOp",EDGE,"E164.10"),sQuery(id+"F15.wireOp",EDGE,"E164.11"),sQuery(id+"F15.wireOp",EDGE,"E164.12"),sQuery(id+"F15.wireOp",EDGE,"E164.13"),sQuery(id+"F15.wireOp",EDGE,"E164.14"),sQuery(id+"F15.wireOp",EDGE,"E164.17")])],"isStart":false});
            var sketch = newSketch(context, id + "F17", { "sketchPlane" : qUnion([Q0])});
            skCircle(sketch, "E165.0", {"center": v(-8, -2.7) * mm, "radius": 1.02 * mm});
            skCircle(sketch, "E166.cCircle", {"center": v(-8, -2.7) * mm, "radius": 2 * mm, "construction": true});
            skLineSegment(sketch, "E166.0", {"start": v(-7.28, -0.83) * mm, "end": v(-6.02, -2.39) * mm});
            skLineSegment(sketch, "E166.1", {"start": v(-6.02, -2.39) * mm, "end": v(-6.74, -4.25) * mm});
            skLineSegment(sketch, "E166.2", {"start": v(-6.74, -4.25) * mm, "end": v(-8.72, -4.56) * mm});
            skLineSegment(sketch, "E166.3", {"start": v(-8.72, -4.56) * mm, "end": v(-9.98, -3) * mm});
            skLineSegment(sketch, "E166.4", {"start": v(-9.98, -3) * mm, "end": v(-9.26, -1.14) * mm});
            skLineSegment(sketch, "E166.5", {"start": v(-9.26, -1.14) * mm, "end": v(-7.28, -0.83) * mm});
            skLineSegment(sketch, "E167.MirrorCS", {"start": v(6.02, -2.39) * mm, "end": v(6.74, -4.25) * mm});
            skLineSegment(sketch, "E168.MirrorCS", {"start": v(6.74, -4.25) * mm, "end": v(8.72, -4.56) * mm});
            skLineSegment(sketch, "E169.MirrorCS", {"start": v(8.72, -4.56) * mm, "end": v(9.98, -3) * mm});
            skLineSegment(sketch, "E170.MirrorCS", {"start": v(9.98, -3) * mm, "end": v(9.26, -1.14) * mm});
            skCircle(sketch, "E171.MirrorC", {"center": v(8, -2.7) * mm, "radius": 1.02 * mm});
            skLineSegment(sketch, "E172.MirrorCS", {"start": v(9.26, -1.14) * mm, "end": v(7.28, -0.83) * mm});
            skLineSegment(sketch, "E173.MirrorCS", {"start": v(7.28, -0.83) * mm, "end": v(6.02, -2.39) * mm});
            skSolve(sketch);
        }
        {
            var Q0;
            Q0=qSketchRegion(id+"F17",true);
            extrude(context, id + "F18", {"entities" : qUnion([Q0]), "depth" : 6 * mm, "offsetDistance" : 25 * mm});
        }
        {
            var Q0;
            Q0=makeQuery(id+"F10.opExtrude","CAP_FACE",FACE,{"disambiguationData":[OSD([sQuery(id+"F9.wireOp",EDGE,"E114.0"),sQuery(id+"F9.wireOp",EDGE,"SBXJPpyz-MpD2-Q15Q-QwKg-3gG3xKiu3ThE")])],"isStart":false});
            var sketch = newSketch(context, id + "F19", { "sketchPlane" : qUnion([Q0])});
            skCircle(sketch, "E174.0", {"center": v(0, 20.84) * mm, "radius": 1.02 * mm});
            skCircle(sketch, "E175.0", {"center": v(-8, -2.7) * mm, "radius": 1.02 * mm});
            skCircle(sketch, "E176.0", {"center": v(8, -2.7) * mm, "radius": 1.02 * mm});
            skFitSpline(sketch, "E177.0", {"points": [v(11.69, 17.5) * mm, v(9.22, 15.05) * mm, v(3.16, 17.26) * mm, v(3.26, 21.6) * mm, v(1, 23.71) * mm, v(0, 23.7) * mm]});
            skFitSpline(sketch, "E178.0", {"points": [v(-11.69, 17.5) * mm, v(-9.22, 15.05) * mm, v(-3.16, 17.26) * mm, v(-3.26, 21.6) * mm, v(-1, 23.71) * mm, v(0, 23.7) * mm]});
            skFitSpline(sketch, "E179", {"points": [v(-3.17, 20.1) * mm, v(-6.22, 2.55) * mm, v(-9.94, -1.38) * mm, v(-10, -4.48) * mm, v(-6.62, -4.96) * mm, v(0, -1.67) * mm], "startDerivative": vector(-10.69, -45.38) * mm, "endDerivative": vector(53.4, 0) * mm});
            skPoint(sketch, "E180.orphan", {"position": v(-23.24, -36.9) * mm});
            skFitSpline(sketch, "E181.MirrorCS", {"points": [v(3.17, 20.1) * mm, v(6.22, 2.55) * mm, v(9.94, -1.38) * mm, v(10, -4.48) * mm, v(6.62, -4.96) * mm, v(0, -1.67) * mm], "startDerivative": vector(10.69, -45.38) * mm, "endDerivative": vector(-53.4, 0) * mm});
            skPoint(sketch, "E182.orphan", {"position": v(-11.69, 17.5) * mm});
            skPoint(sketch, "E183.orphan", {"position": v(11.69, 17.5) * mm});
            skPoint(sketch, "E184.orphan", {"position": v(23.24, -36.9) * mm});
            skFitSpline(sketch, "E185", {"points": [v(4.93, -0.49) * mm, v(0, 3.98) * mm, v(-4.93, -0.49) * mm, v(0, 0.74) * mm, v(4.93, -0.49) * mm], "construction": true});
            skFitSpline(sketch, "E186", {"points": [v(0, 10.71) * mm, v(-3.18, 5.62) * mm, v(0, 6.41) * mm, v(3.18, 5.62) * mm, v(0, 10.71) * mm], "construction": true});
            skFitSpline(sketch, "E187", {"points": [v(0, 16.44) * mm, v(-2.3, 12.53) * mm, v(0, 13.04) * mm, v(2.3, 12.53) * mm, v(0, 16.44) * mm], "construction": true});
            skSolve(sketch);
        }
        {
            var Q0;
            Q0=qSketchRegion(id+"F19",true);
            extrude(context, id + "F20", {"entities" : qUnion([Q0]), "depth" : 1.5 * mm, "offsetDistance" : 25 * mm});
        }
        {
            var Q0;
            Q0=makeQuery(id+"F9.imprint","IMPRINT",FACE,{"disambiguationData":[TD([[makeQuery(id+"F9.imprint","IMPRINT",EDGE,{"derivedFrom":sQuery(id+"F9.wireOp",EDGE,"E115.0")}),1.0]])]});
            cPlane(context, id + "F21", {"entities" : qUnion([Q0]), "cplaneType" : CPlaneType.OFFSET, "offset" : 9 * mm, "width" : 150 * mm, "height" : 150 * mm});
        }
        {
            var Q0;
            Q0=qCreatedBy(id+"F21.planeOp",FACE);
            var sketch = newSketch(context, id + "F22", { "sketchPlane" : qUnion([Q0])});
            skCircle(sketch, "E188.0", {"center": v(-30.04, -36.9) * mm, "radius": 25.4 * mm});
            skCircle(sketch, "E189.0", {"center": v(30.04, -36.9) * mm, "radius": 25.4 * mm});
            skCircle(sketch, "E190.0", {"center": v(30.04, 36.9) * mm, "radius": 25.4 * mm});
            skCircle(sketch, "E191.0", {"center": v(-30.04, 36.9) * mm, "radius": 25.4 * mm});
            skSolve(sketch);
        }
        {
            var Q0;
            Q0=qSketchRegion(id+"F22",true);
            extrude(context, id + "F23", {"entities" : qUnion([Q0]), "depth" : 2 * mm, "offsetDistance" : 25 * mm});
        }
        {
            var Q0;
            Q0=makeQuery(id+"F6.opExtrude","CAP_FACE",FACE,{"disambiguationData":[OSD([sQuery(id+"F5.wireOp",EDGE,"E10"),sQuery(id+"F5.wireOp",EDGE,"E11"),sQuery(id+"F5.wireOp",EDGE,"E12"),sQuery(id+"F5.wireOp",EDGE,"E13"),sQuery(id+"F5.wireOp",EDGE,"E14"),sQuery(id+"F5.wireOp",EDGE,"E15"),sQuery(id+"F5.wireOp",EDGE,"E16"),sQuery(id+"F5.wireOp",EDGE,"E17"),sQuery(id+"F5.wireOp",EDGE,"E18.MirrorC"),sQuery(id+"F5.wireOp",EDGE,"E19.MirrorC"),sQuery(id+"F5.wireOp",EDGE,"E20.MirrorC"),sQuery(id+"F5.wireOp",EDGE,"E21.MirrorC"),sQuery(id+"F5.wireOp",EDGE,"E25.MirrorC"),sQuery(id+"F5.wireOp",EDGE,"E26.MirrorC"),sQuery(id+"F5.wireOp",EDGE,"E27.MirrorC"),sQuery(id+"F5.wireOp",EDGE,"E28.MirrorC"),sQuery(id+"F5.wireOp",EDGE,"E29.MirrorC"),sQuery(id+"F5.wireOp",EDGE,"E30"),sQuery(id+"F5.wireOp",EDGE,"E31"),sQuery(id+"F5.wireOp",EDGE,"E32"),sQuery(id+"F5.wireOp",EDGE,"E33"),sQuery(id+"F5.wireOp",EDGE,"E34.filletArc"),sQuery(id+"F5.wireOp",EDGE,"E35.filletArc"),sQuery(id+"F5.wireOp",EDGE,"E36.MirrorCS"),sQuery(id+"F5.wireOp",EDGE,"E37.MirrorCS"),sQuery(id+"F5.wireOp",EDGE,"E38.MirrorCS"),sQuery(id+"F5.wireOp",EDGE,"E39.MirrorCS"),sQuery(id+"F5.wireOp",EDGE,"E40.MirrorCS"),sQuery(id+"F5.wireOp",EDGE,"E41.MirrorCS"),sQuery(id+"F5.wireOp",EDGE,"E42"),sQuery(id+"F5.wireOp",EDGE,"E43.MirrorC"),sQuery(id+"F5.wireOp",EDGE,"E23.MirrorC"),sQuery(id+"F5.wireOp",EDGE,"E44.MirrorCS"),sQuery(id+"F5.wireOp",EDGE,"E22.MirrorC"),sQuery(id+"F5.wireOp",EDGE,"E24.MirrorC"),sQuery(id+"F5.wireOp",EDGE,"E45.MirrorCS"),sQuery(id+"F5.wireOp",EDGE,"E46.MirrorCS"),sQuery(id+"F5.wireOp",EDGE,"E47.MirrorCS"),sQuery(id+"F5.wireOp",EDGE,"E48.MirrorCS"),sQuery(id+"F5.wireOp",EDGE,"E49.MirrorCS"),sQuery(id+"F5.wireOp",EDGE,"E50.MirrorC"),sQuery(id+"F5.wireOp",EDGE,"E51.MirrorCS"),sQuery(id+"F5.wireOp",EDGE,"E52.MirrorCS"),sQuery(id+"F5.wireOp",EDGE,"E53.MirrorCS"),sQuery(id+"F5.wireOp",EDGE,"E54.MirrorCS"),sQuery(id+"F5.wireOp",EDGE,"E55.MirrorCS"),sQuery(id+"F5.wireOp",EDGE,"E56.MirrorCS"),sQuery(id+"F5.wireOp",EDGE,"E57.MirrorC"),sQuery(id+"F5.wireOp",EDGE,"E58"),sQuery(id+"F5.wireOp",EDGE,"E59.MirrorC"),sQuery(id+"F5.wireOp",EDGE,"E60.MirrorC"),sQuery(id+"F5.wireOp",EDGE,"E61"),sQuery(id+"F5.wireOp",EDGE,"E62"),sQuery(id+"F5.wireOp",EDGE,"E64.MirrorC"),sQuery(id+"F5.wireOp",EDGE,"E65.MirrorC"),sQuery(id+"F5.wireOp",EDGE,"E66.MirrorC"),sQuery(id+"F5.wireOp",EDGE,"E67.MirrorC"),sQuery(id+"F5.wireOp",EDGE,"E68.MirrorC"),sQuery(id+"F5.wireOp",EDGE,"E69.MirrorC"),sQuery(id+"F5.wireOp",EDGE,"E70"),sQuery(id+"F5.wireOp",EDGE,"E71"),sQuery(id+"F5.wireOp",EDGE,"E72.MirrorCS"),sQuery(id+"F5.wireOp",EDGE,"E82.MirrorC"),sQuery(id+"F5.wireOp",EDGE,"E83")])],"isStart":true});
            var sketch = newSketch(context, id + "F24", { "sketchPlane" : qUnion([Q0])});
            skLineSegment(sketch, "E192.bottom", {"start": v(-10, 14.07) * mm, "end": v(10, 14.07) * mm});
            skLineSegment(sketch, "E192.top", {"start": v(-10, -17.93) * mm, "end": v(10, -17.93) * mm});
            skLineSegment(sketch, "E192.left", {"start": v(-10, 14.07) * mm, "end": v(-10, -17.93) * mm});
            skLineSegment(sketch, "E192.right", {"start": v(10, 14.07) * mm, "end": v(10, -17.93) * mm});
            skPoint(sketch, "E193", {"position": v(0, 14.07) * mm});
            skSolve(sketch);
        }
        {
            var Q0;
            Q0=qSketchRegion(id+"F24",true);
            extrude(context, id + "F25", {"entities" : qUnion([Q0]), "depth" : 7 * mm, "offsetDistance" : 25 * mm});
        }
        {
            var Q0;
            Q0=makeQuery(id+"F6.opExtrude","CAP_FACE",FACE,{"disambiguationData":[OSD([sQuery(id+"F5.wireOp",EDGE,"E10"),sQuery(id+"F5.wireOp",EDGE,"E11"),sQuery(id+"F5.wireOp",EDGE,"E12"),sQuery(id+"F5.wireOp",EDGE,"E13"),sQuery(id+"F5.wireOp",EDGE,"E14"),sQuery(id+"F5.wireOp",EDGE,"E15"),sQuery(id+"F5.wireOp",EDGE,"E16"),sQuery(id+"F5.wireOp",EDGE,"E17"),sQuery(id+"F5.wireOp",EDGE,"E18.MirrorC"),sQuery(id+"F5.wireOp",EDGE,"E19.MirrorC"),sQuery(id+"F5.wireOp",EDGE,"E20.MirrorC"),sQuery(id+"F5.wireOp",EDGE,"E21.MirrorC"),sQuery(id+"F5.wireOp",EDGE,"E25.MirrorC"),sQuery(id+"F5.wireOp",EDGE,"E26.MirrorC"),sQuery(id+"F5.wireOp",EDGE,"E27.MirrorC"),sQuery(id+"F5.wireOp",EDGE,"E28.MirrorC"),sQuery(id+"F5.wireOp",EDGE,"E29.MirrorC"),sQuery(id+"F5.wireOp",EDGE,"E30"),sQuery(id+"F5.wireOp",EDGE,"E31"),sQuery(id+"F5.wireOp",EDGE,"E32"),sQuery(id+"F5.wireOp",EDGE,"E33"),sQuery(id+"F5.wireOp",EDGE,"E34.filletArc"),sQuery(id+"F5.wireOp",EDGE,"E35.filletArc"),sQuery(id+"F5.wireOp",EDGE,"E36.MirrorCS"),sQuery(id+"F5.wireOp",EDGE,"E37.MirrorCS"),sQuery(id+"F5.wireOp",EDGE,"E38.MirrorCS"),sQuery(id+"F5.wireOp",EDGE,"E39.MirrorCS"),sQuery(id+"F5.wireOp",EDGE,"E40.MirrorCS"),sQuery(id+"F5.wireOp",EDGE,"E41.MirrorCS"),sQuery(id+"F5.wireOp",EDGE,"E42"),sQuery(id+"F5.wireOp",EDGE,"E43.MirrorC"),sQuery(id+"F5.wireOp",EDGE,"E23.MirrorC"),sQuery(id+"F5.wireOp",EDGE,"E44.MirrorCS"),sQuery(id+"F5.wireOp",EDGE,"E22.MirrorC"),sQuery(id+"F5.wireOp",EDGE,"E24.MirrorC"),sQuery(id+"F5.wireOp",EDGE,"E45.MirrorCS"),sQuery(id+"F5.wireOp",EDGE,"E46.MirrorCS"),sQuery(id+"F5.wireOp",EDGE,"E47.MirrorCS"),sQuery(id+"F5.wireOp",EDGE,"E48.MirrorCS"),sQuery(id+"F5.wireOp",EDGE,"E49.MirrorCS"),sQuery(id+"F5.wireOp",EDGE,"E50.MirrorC"),sQuery(id+"F5.wireOp",EDGE,"E51.MirrorCS"),sQuery(id+"F5.wireOp",EDGE,"E52.MirrorCS"),sQuery(id+"F5.wireOp",EDGE,"E53.MirrorCS"),sQuery(id+"F5.wireOp",EDGE,"E54.MirrorCS"),sQuery(id+"F5.wireOp",EDGE,"E55.MirrorCS"),sQuery(id+"F5.wireOp",EDGE,"E56.MirrorCS"),sQuery(id+"F5.wireOp",EDGE,"E57.MirrorC"),sQuery(id+"F5.wireOp",EDGE,"E58"),sQuery(id+"F5.wireOp",EDGE,"E59.MirrorC"),sQuery(id+"F5.wireOp",EDGE,"E60.MirrorC"),sQuery(id+"F5.wireOp",EDGE,"E61"),sQuery(id+"F5.wireOp",EDGE,"E62"),sQuery(id+"F5.wireOp",EDGE,"E64.MirrorC"),sQuery(id+"F5.wireOp",EDGE,"E65.MirrorC"),sQuery(id+"F5.wireOp",EDGE,"E66.MirrorC"),sQuery(id+"F5.wireOp",EDGE,"E67.MirrorC"),sQuery(id+"F5.wireOp",EDGE,"E68.MirrorC"),sQuery(id+"F5.wireOp",EDGE,"E69.MirrorC"),sQuery(id+"F5.wireOp",EDGE,"E70"),sQuery(id+"F5.wireOp",EDGE,"E71"),sQuery(id+"F5.wireOp",EDGE,"E72.MirrorCS"),sQuery(id+"F5.wireOp",EDGE,"E82.MirrorC"),sQuery(id+"F5.wireOp",EDGE,"E83"),sQuery(id+"F5.wireOp",EDGE,"E84"),sQuery(id+"F5.wireOp",EDGE,"E86.MirrorCS"),sQuery(id+"F5.wireOp",EDGE,"E87"),sQuery(id+"F5.wireOp",EDGE,"E88")])],"isStart":true});
            var sketch = newSketch(context, id + "F26", { "sketchPlane" : qUnion([Q0])});
            skPoint(sketch, "E194.orphan", {"position": v(-29.41, 28.73) * mm});
            skLineSegment(sketch, "E195", {"start": v(-29.5, 35.18) * mm, "end": v(-34.88, 44.28) * mm, "construction": true});
            skFitSpline(sketch, "E196.0", {"points": [v(-31.4, 38.1) * mm, v(-32.21, 37.63) * mm, v(-34.68, 38.02) * mm, v(-32.37, 40.82) * mm, v(-29.73, 40.79) * mm, v(-30.54, 38.58) * mm, v(-31.4, 38.1) * mm]});
            skSolve(sketch);
        }
        {
            var Q0;
            Q0=makeQuery(id+"F6.opExtrude","CAP_FACE",FACE,{"disambiguationData":[OSD([sQuery(id+"F5.wireOp",EDGE,"E10"),sQuery(id+"F5.wireOp",EDGE,"E11"),sQuery(id+"F5.wireOp",EDGE,"E12"),sQuery(id+"F5.wireOp",EDGE,"E13"),sQuery(id+"F5.wireOp",EDGE,"E14"),sQuery(id+"F5.wireOp",EDGE,"E15"),sQuery(id+"F5.wireOp",EDGE,"E16"),sQuery(id+"F5.wireOp",EDGE,"E17"),sQuery(id+"F5.wireOp",EDGE,"E18.MirrorC"),sQuery(id+"F5.wireOp",EDGE,"E19.MirrorC"),sQuery(id+"F5.wireOp",EDGE,"E20.MirrorC"),sQuery(id+"F5.wireOp",EDGE,"E21.MirrorC"),sQuery(id+"F5.wireOp",EDGE,"E25.MirrorC"),sQuery(id+"F5.wireOp",EDGE,"E26.MirrorC"),sQuery(id+"F5.wireOp",EDGE,"E27.MirrorC"),sQuery(id+"F5.wireOp",EDGE,"E28.MirrorC"),sQuery(id+"F5.wireOp",EDGE,"E29.MirrorC"),sQuery(id+"F5.wireOp",EDGE,"E30"),sQuery(id+"F5.wireOp",EDGE,"E31"),sQuery(id+"F5.wireOp",EDGE,"E32"),sQuery(id+"F5.wireOp",EDGE,"E33"),sQuery(id+"F5.wireOp",EDGE,"E34.filletArc"),sQuery(id+"F5.wireOp",EDGE,"E35.filletArc"),sQuery(id+"F5.wireOp",EDGE,"E36.MirrorCS"),sQuery(id+"F5.wireOp",EDGE,"E37.MirrorCS"),sQuery(id+"F5.wireOp",EDGE,"E38.MirrorCS"),sQuery(id+"F5.wireOp",EDGE,"E39.MirrorCS"),sQuery(id+"F5.wireOp",EDGE,"E40.MirrorCS"),sQuery(id+"F5.wireOp",EDGE,"E41.MirrorCS"),sQuery(id+"F5.wireOp",EDGE,"E42"),sQuery(id+"F5.wireOp",EDGE,"E43.MirrorC"),sQuery(id+"F5.wireOp",EDGE,"E23.MirrorC"),sQuery(id+"F5.wireOp",EDGE,"E44.MirrorCS"),sQuery(id+"F5.wireOp",EDGE,"E22.MirrorC"),sQuery(id+"F5.wireOp",EDGE,"E24.MirrorC"),sQuery(id+"F5.wireOp",EDGE,"E45.MirrorCS"),sQuery(id+"F5.wireOp",EDGE,"E46.MirrorCS"),sQuery(id+"F5.wireOp",EDGE,"E47.MirrorCS"),sQuery(id+"F5.wireOp",EDGE,"E48.MirrorCS"),sQuery(id+"F5.wireOp",EDGE,"E49.MirrorCS"),sQuery(id+"F5.wireOp",EDGE,"E50.MirrorC"),sQuery(id+"F5.wireOp",EDGE,"E51.MirrorCS"),sQuery(id+"F5.wireOp",EDGE,"E52.MirrorCS"),sQuery(id+"F5.wireOp",EDGE,"E53.MirrorCS"),sQuery(id+"F5.wireOp",EDGE,"E54.MirrorCS"),sQuery(id+"F5.wireOp",EDGE,"E55.MirrorCS"),sQuery(id+"F5.wireOp",EDGE,"E56.MirrorCS"),sQuery(id+"F5.wireOp",EDGE,"E57.MirrorC"),sQuery(id+"F5.wireOp",EDGE,"E58"),sQuery(id+"F5.wireOp",EDGE,"E59.MirrorC"),sQuery(id+"F5.wireOp",EDGE,"E60.MirrorC"),sQuery(id+"F5.wireOp",EDGE,"E61"),sQuery(id+"F5.wireOp",EDGE,"E62"),sQuery(id+"F5.wireOp",EDGE,"E64.MirrorC"),sQuery(id+"F5.wireOp",EDGE,"E65.MirrorC"),sQuery(id+"F5.wireOp",EDGE,"E66.MirrorC"),sQuery(id+"F5.wireOp",EDGE,"E67.MirrorC"),sQuery(id+"F5.wireOp",EDGE,"E68.MirrorC"),sQuery(id+"F5.wireOp",EDGE,"E69.MirrorC"),sQuery(id+"F5.wireOp",EDGE,"E70"),sQuery(id+"F5.wireOp",EDGE,"E71"),sQuery(id+"F5.wireOp",EDGE,"E72.MirrorCS"),sQuery(id+"F5.wireOp",EDGE,"E82.MirrorC"),sQuery(id+"F5.wireOp",EDGE,"E83"),sQuery(id+"F5.wireOp",EDGE,"E84"),sQuery(id+"F5.wireOp",EDGE,"E86.MirrorCS"),sQuery(id+"F5.wireOp",EDGE,"E87"),sQuery(id+"F5.wireOp",EDGE,"E88")])],"isStart":false});
            var sketch = newSketch(context, id + "F27", { "sketchPlane" : qUnion([Q0])});
            skPoint(sketch, "E197.0", {"position": v(-29.5, -35.18) * mm});
            skSolve(sketch);
        }
        {
            var Q0;
            Q0 = qSketchRegion(id + "F26", true);
            extrude(context, id + "F28", {"entities" : qUnion([Q0]), "depth" : 2 * mm, "offsetDistance" : 25 * mm, "hasSecondDirection" : true, "secondDirectionOppositeDirection" : true, "secondDirectionDepth" : 3 * mm});
        }
        {
            var Q0;
            Q0=sQuery(id+"F26.wireOp",VERTEX,"E195.end");
            var Q1;
            Q1=sQuery(id+"F26.wireOp",VERTEX,"E195.start");
            var Q2;
            Q2=sQuery(id+"F27.wireOp",VERTEX,"E197.0");
            cPlane(context, id + "F29", {"entities" : qUnion([Q0, Q1, Q2]), "cplaneType" : CPlaneType.THREE_POINT, "offset" : 25 * mm, "width" : 150 * mm, "height" : 150 * mm});
        }
        {
            var Q0;
            Q0=qCreatedBy(id+"F29.planeOp",FACE);
            var sketch = newSketch(context, id + "F30", { "sketchPlane" : qUnion([Q0])});
            skFitSpline(sketch, "E198", {"points": [v(50.1, -2) * mm, v(54.86, -2.01) * mm, v(63.4, -1.19) * mm, v(75.98, 5.86) * mm, v(78.12, 10.87) * mm], "startDerivative": vector(21.09, -0.8) * mm, "endDerivative": vector(2.09, 20.87) * mm});
            skFitSpline(sketch, "E199", {"points": [v(50.1, 0) * mm, v(55.75, -0.13) * mm, v(61.24, 0) * mm, v(72.27, 4.68) * mm, v(75.69, 8.65) * mm, v(76.12, 10.87) * mm], "startDerivative": vector(47.54, 0) * mm, "endDerivative": vector(2, 15.27) * mm});
            skLineSegment(sketch, "E200", {"start": v(78.12, 10.87) * mm, "end": v(76.12, 10.87) * mm});
            skLineSegment(sketch, "E201", {"start": v(50.1, -2) * mm, "end": v(50.1, 0) * mm});
            skPoint(sketch, "E202.orphan", {"position": v(39.7, 2) * mm});
            skSolve(sketch);
        }
        {
            var Q0;
            Q0=makeQuery(id+"F30.imprint","IMPRINT",FACE,{"disambiguationData":[TD([[makeQuery(id+"F30.imprint","IMPRINT",EDGE,{"derivedFrom":sQuery(id+"F30.wireOp",EDGE,"E198")}),1.0]])]});
            extrude(context, id + "F31", {"entities" : qUnion([Q0]), "operationType" : NewBodyOperationType.ADD, "depth" : 1.95 * mm, "offsetDistance" : 25 * mm, "hasSecondDirection" : true, "secondDirectionOppositeDirection" : true, "secondDirectionDepth" : 1.84 * mm});
        }
        {
            var Q0;
            Q0=makeQuery(id+"F31.opExtrude","CAP_FACE",FACE,{"disambiguationData":[OSD([sQuery(id+"F30.wireOp",EDGE,"E198"),sQuery(id+"F30.wireOp",EDGE,"E199"),sQuery(id+"F30.wireOp",EDGE,"E200"),sQuery(id+"F30.wireOp",EDGE,"E201")])],"isStart":false});
            var sketch = newSketch(context, id + "F32", { "sketchPlane" : qUnion([Q0])});
            skCircle(sketch, "E203", {"center": v(77.13, 11.61) * mm, "radius": 0.4 * mm});
            skCircle(sketch, "E204", {"center": v(77.13, 11.61) * mm, "radius": 1.24 * mm});
            skSolve(sketch);
        }
        {
            var Q0;
            Q0=makeQuery(id+"F32.imprint","IMPRINT",FACE,{"disambiguationData":[TD([[makeQuery(id+"F32.imprint","IMPRINT",EDGE,{"derivedFrom":sQuery(id+"F32.wireOp",EDGE,"E203")}),-1.0]])]});
            var Q1;
            Q1=makeQuery(id+"F31.opExtrude","CAP_FACE",FACE,{"disambiguationData":[OSD([sQuery(id+"F30.wireOp",EDGE,"E198"),sQuery(id+"F30.wireOp",EDGE,"E199"),sQuery(id+"F30.wireOp",EDGE,"E200"),sQuery(id+"F30.wireOp",EDGE,"E201")])],"isStart":true});
            extrude(context, id + "F33", {"entities" : qUnion([Q0]), "operationType" : NewBodyOperationType.ADD, "endBound" : BoundingType.UP_TO_SURFACE, "oppositeDirection" : true, "depth" : 3.78 * mm, "endBoundEntityFace" : qUnion([Q1]), "offsetDistance" : 25 * mm});
        }
        {
            var Q0;
            Q0=makeQuery(id+"F27.imprint","IMPRINT",FACE,{"disambiguationData":[TD([[makeQuery(id+"F27.imprint","IMPRINT",EDGE,{"derivedFrom":makeQuery(id+"F6.opExtrude","CAP_EDGE",EDGE,{"disambiguationData":[OSD([sQuery(id+"F5.wireOp",EDGE,"E10")])],"isStart":false})}),-1.0]])]});
            var sketch = newSketch(context, id + "F34", { "sketchPlane" : qUnion([Q0])});
            skFitSpline(sketch, "E205", {"points": [v(-32.43, -39.51) * mm, v(-31.53, -39.98) * mm, v(-31.03, -39.9) * mm, v(-31.3, -39.1) * mm, v(-32.03, -38.59) * mm, v(-32.9, -38.65) * mm, v(-32.43, -39.51) * mm]});
            skSolve(sketch);
        }
        {
            var Q0;
            Q0=makeQuery(id+"F27.imprint","IMPRINT",FACE,{"disambiguationData":[TD([[makeQuery(id+"F27.imprint","IMPRINT",EDGE,{"derivedFrom":makeQuery(id+"F6.opExtrude","CAP_EDGE",EDGE,{"disambiguationData":[OSD([sQuery(id+"F5.wireOp",EDGE,"E10")])],"isStart":false})}),-1.0]])]});
            var sketch = newSketch(context, id + "F35", { "sketchPlane" : qUnion([Q0])});
            skFitSpline(sketch, "E206", {"points": [v(-33.7, -38.54) * mm, v(-33.86, -40.07) * mm, v(-32.07, -41.36) * mm, v(-30.52, -40.48) * mm], "startDerivative": vector(-2.26, -5.44) * mm, "endDerivative": vector(3.84, 5.06) * mm});
            skFitSpline(sketch, "E207", {"points": [v(-33.7, -38.54) * mm, v(-31.6, -38.75) * mm, v(-30.52, -40.48) * mm], "startDerivative": vector(3.77, 2.55) * mm, "endDerivative": vector(-0.15, -3.06) * mm});
            skSolve(sketch);
        }
        {
            var Q0;
            Q0 = qSketchRegion(id + "F35", true);
            extrude(context, id + "F36", {"entities" : qUnion([Q0]), "operationType" : NewBodyOperationType.ADD, "depth" : 1 * mm, "offsetDistance" : 25 * mm});
        }
        {
            var Q0;
            Q0=makeQuery(id+"F28.opExtrude","CAP_EDGE",EDGE,{"disambiguationData":[OSD([sQuery(id+"F26.wireOp",EDGE,"E196.0")])],"isStart":true});
            var Q1;
            Q1=makeQuery(id+"F36.opExtrude","CAP_EDGE",EDGE,{"disambiguationData":[OSD([sQuery(id+"F35.wireOp",EDGE,"E206")])],"isStart":false});
            fillet(context, id + "F37", {"entities" : qUnion([Q0, Q1]), "radius" : 0.5 * mm, "tangentPropagation" : true, "allowEdgeOverflow" : false});
        }
        {
            var Q0;
            Q0 = qSketchRegion(id + "F34", true);
            extrude(context, id + "F38", {"entities" : qUnion([Q0]), "operationType" : NewBodyOperationType.REMOVE, "endBound" : BoundingType.THROUGH_ALL, "depth" : 25 * mm, "offsetDistance" : 25 * mm, "hasSecondDirection" : true, "secondDirectionOppositeDirection" : true, "secondDirectionDepth" : getVariable(context, 'PlateThickness') / 2});
        }
        {
            var Q0;
            {var subQ0=sQuery(id+"F30.wireOp",EDGE,"E200");var subQ1=sQuery(id+"F30.wireOp",EDGE,"E199");Q0=makeQuery(id+"F33.boolean.opBoolean","MERGE",EDGE,{"derivedFrom":[makeQuery(id+"F31.opExtrude","SWEPT_EDGE",EDGE,{"disambiguationData":[OSD([subQ1,subQ0])]}),makeQuery(id+"F33.opExtrude","SWEPT_EDGE",EDGE,{"disambiguationData":[OSD([subQ1,subQ0,sQuery(id+"F32.wireOp",EDGE,"E204")])]})]});}
            var Q1;
            Q1=makeQuery(id+"F33.opExtrude","SWEPT_EDGE",EDGE,{"disambiguationData":[OSD([sQuery(id+"F30.wireOp",EDGE,"E198"),sQuery(id+"F32.wireOp",EDGE,"E204")])]});
            fillet(context, id + "F39", {"entities" : qUnion([Q0, Q1]), "radius" : 5 * mm, "tangentPropagation" : true, "allowEdgeOverflow" : false});
        }
    });
